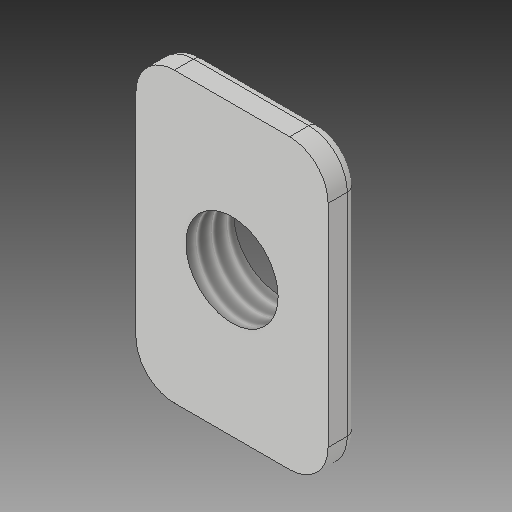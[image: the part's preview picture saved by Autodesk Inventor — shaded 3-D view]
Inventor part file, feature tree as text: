
AUTODESK INVENTOR PART (.ipt)
format: ipt  version: 2017 (Build 210142000, 142)  size: 143,872 bytes
history: native  units: mm
features: other x3, sketch x2
ambient origin geometry x8: Origin, YZ Plane, XZ Plane, XY Plane, X Axis, Y Axis, Z Axis, Center Point
bodies: Solid1 (feature_tree)
feature tree (5):
  other  "M5 Tee Nut_MIR_MIR.ipt"
  other  "Solid1::M5 Tee Nut_MIR_MIR.ipt"
  other  "TaggingFeature1"
  sketch  "Sketch1"  dims[d0=10.0mm]
  sketch  "Sketch2"
